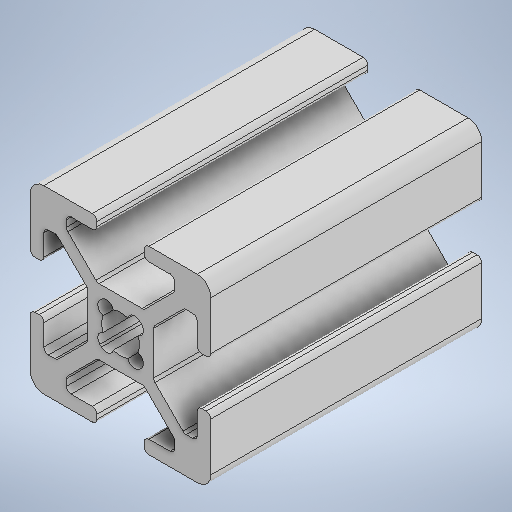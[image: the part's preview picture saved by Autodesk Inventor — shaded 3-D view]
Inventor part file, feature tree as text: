
AUTODESK INVENTOR PART (.ipt)
format: ipt  version: 2025 (Build 290162000, 162)  size: 363,008 bytes
history: native  units: mm
features: extrude x1, sketch x1
ambient origin geometry x8: Origin, YZ Plane, XZ Plane, XY Plane, X Axis, Y Axis, Z Axis, Center Point
bodies: Solid1 (feature_tree)
feature tree (2):
  extrude  "Extrusion1"  Depth=30.0mm
  sketch  "Sketch1"  dims[d0=30.0mm d1=0.0mm d2=1.0mm d3=1.0mm d4=1.0mm d5=0.15mm d6=0.25mm d7=0.375mm d8=14.3117mm d9=0.75mm d10=20.594885mm d11=0.0625mm d12=0.75mm d13=0.375mm]
